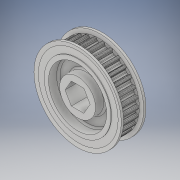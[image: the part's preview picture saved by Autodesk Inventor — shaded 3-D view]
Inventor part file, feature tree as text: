
AUTODESK INVENTOR PART (.ipt)
format: ipt  version: 2017 (Build 210142000, 142)  size: 918,016 bytes
history: native  units: in
note: dims shown in document units (in); Inventor stores cm internally (conversion verified against a paired STEP export)
features: mirror x1
ambient origin geometry x8: Origin, YZ Plane, XZ Plane, XY Plane, X Axis, Y Axis, Z Axis, Center Point
bodies: Solid1 (feature_tree)
feature tree (1):
  mirror  "Mirror1"
